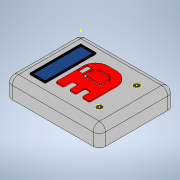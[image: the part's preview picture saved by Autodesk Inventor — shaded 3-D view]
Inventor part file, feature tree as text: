
AUTODESK INVENTOR PART (.ipt)
format: ipt  version: 2020 (Build 240168000, 168)  size: 358,912 bytes
history: native  units: in
note: dims shown in document units (in); Inventor stores cm internally (conversion verified against a paired STEP export)
features: sketch x9, extrude x6, fillet x5, projected_geometry x1
ambient origin geometry x8: Origin, YZ Plane, XZ Plane, XY Plane, X Axis, Y Axis, Z Axis, Center Point
bodies: Solid1 (feature_tree)
feature tree (21):
  extrude  "Extrusion1"  Depth=120.0in
  extrude  "Extrusion2"  Depth=82.0in
  sketch  "Sketch3"  dims[d6=19.0in d7=19.0in d8=25.0in d9=2.0in d10=0.0in]
  extrude  "Extrusion3"  Depth=19.0in
  fillet  "Fillet1"  Radius=25.0in
  fillet  "Fillet2"  Radius=2.0in
  extrude  "Extrusion4"  Depth=2.0in
  extrude  "Extrusion5"  Depth=2.0in
  sketch  "Sketch7"  dims[d21=20.0in]
  extrude  "Extrusion6"  Depth=10.0in
  fillet  "Fillet3"  Radius=10.0in
  fillet  "Fillet4"  Radius=10.0in
  fillet  "Fillet5"  Radius=20.0in
  sketch  "Sketch10"  dims[d23=10.0in d24=0.0in d25=2.0in d26=2.0in d27=1.0in d28=1.0in d29=1.0in d30=1.0in d31=2.0in d32=2.0in d33=4.0in d34=0.0in d35=64.0in d36=54.0in d37=28.0in d38=8.0in d39=12.0in d40=12.0in d41=10.0in d42=10.0in d43=15.0in d44=15.0in d45=12.0in d46=15.0in d47=3.0in d48=3.0in d49=3.0in d50=3.0in d51=2.0in d52=2.0in d53=2.0in d54=0.0in d55=20.0in d56=10.0in d57=2.0in]
  sketch  "Sketch1"  dims[d0=150.0in d1=120.0in]
  sketch  "Sketch2"  dims[d2=30.0in d3=0.0in d5=82.0in]
  sketch  "Sketch4"  dims[d11=2.0in d12=2.0in]
  sketch  "Sketch5"  dims[d13=2.0in d14=2.0in]
  sketch  "Sketch6"  dims[d15=2.0in d16=0.0in d17=10.0in d18=10.0in d19=10.0in d20=20.0in]
  projected_geometry  "Projected Loop1"
  sketch  "Sketch9"  dims[d22=20.0in]
